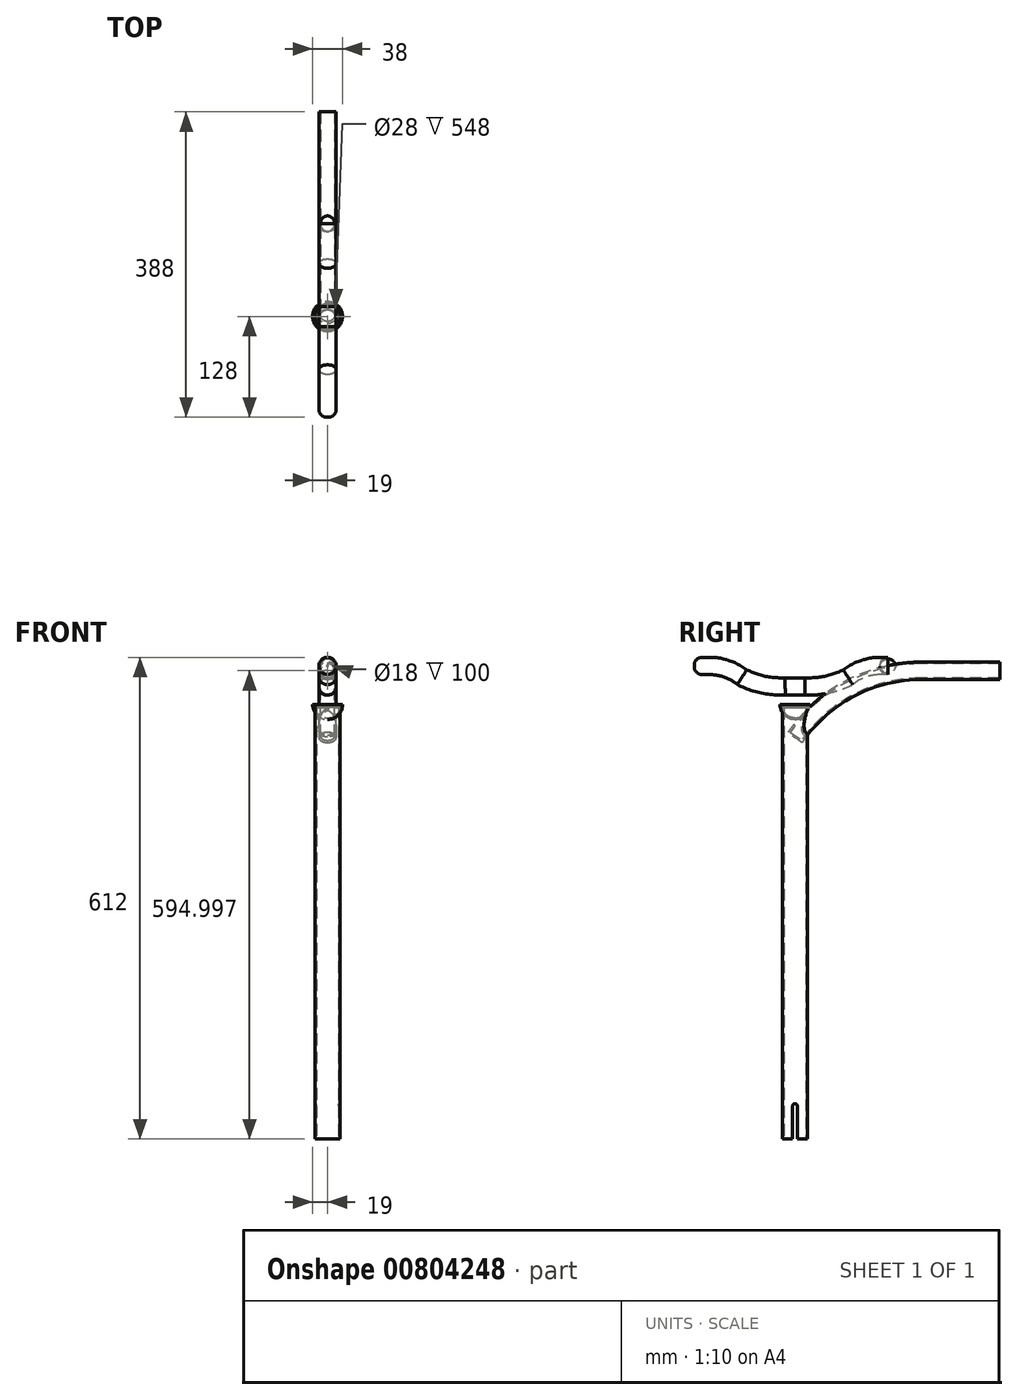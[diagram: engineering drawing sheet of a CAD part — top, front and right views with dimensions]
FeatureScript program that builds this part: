
annotation { "Feature Type Name" : "Feature", "Feature Type Description" : "" }
export const myFeature = defineFeature(function(context is Context, id is Id, definition is map)
    precondition{}
    {
        {
            var Q0;
            Q0=qCreatedBy(makeId("Top.planeOp"),FACE);
            var sketch = newSketch(context, id + "F0", { "sketchPlane" : qUnion([Q0])});
            skCircle(sketch, "E0", {"center": v(0, 0) * mm, "radius": 16 * mm});
            skSolve(sketch);
        }
        {
            var Q0;
            Q0 = qSketchRegion(id + "F0", true);
            extrude(context, id + "F1", {"entities" : qUnion([Q0]), "depth" : 550 * mm, "offsetDistance" : 25 * mm});
        }
        {
            var Q0;
            Q0=makeQuery(id+"F1.opExtrude","CAP_FACE",FACE,{"disambiguationData":[OSD([sQuery(id+"F0.wireOp",EDGE,"E0")])],"isStart":true});
            shell(context, id + "F2", {"entities" : qUnion([Q0]), "thickness" : 2 * mm});
        }
        {
            var Q0;
            Q0=qCreatedBy(makeId("Right.planeOp"),FACE);
            var sketch = newSketch(context, id + "F3", { "sketchPlane" : qUnion([Q0])});
            skLineSegment(sketch, "E1.bottom", {"start": v(-3, 0) * mm, "end": v(3, 0) * mm});
            skLineSegment(sketch, "E1.top", {"start": v(0, 45) * mm, "end": v(0, 45) * mm});
            skLineSegment(sketch, "E1.left", {"start": v(-3, 0) * mm, "end": v(-3, 42) * mm});
            skLineSegment(sketch, "E1.right", {"start": v(3, 0) * mm, "end": v(3, 42) * mm});
            skPoint(sketch, "E2.visualSharp", {"position": v(-3, 45) * mm});
            skArc(sketch, "E2.filletArc", {"start": v(0, 45) * mm, "mid": v(-2.12, 44.12) * mm, "end": v(-3, 42) * mm});
            skPoint(sketch, "E3.visualSharp", {"position": v(3, 45) * mm});
            skArc(sketch, "E3.filletArc", {"start": v(3, 42) * mm, "mid": v(2.12, 44.12) * mm, "end": v(0, 45) * mm});
            skSolve(sketch);
        }
        {
            var Q0;
            Q0 = qSketchRegion(id + "F3", true);
            extrude(context, id + "F4", {"entities" : qUnion([Q0]), "operationType" : NewBodyOperationType.REMOVE, "endBound" : BoundingType.SYMMETRIC, "depth" : 35 * mm, "offsetDistance" : 25 * mm});
        }
        {
            var Q0;
            Q0=qCreatedBy(makeId("Right.planeOp"),FACE);
            var sketch = newSketch(context, id + "F5", { "sketchPlane" : qUnion([Q0])});
            skArc(sketch, "E4", {"start": v(160, 595) * mm, "mid": v(69.53, 572.2) * mm, "end": v(0, 510) * mm});
            skLineSegment(sketch, "E5", {"start": v(160, 595) * mm, "end": v(260, 595) * mm});
            skLineSegment(sketch, "E6", {"start": v(0, 550) * mm, "end": v(0, 510) * mm, "construction": true});
            skSolve(sketch);
        }
        {
            var Q0;
            Q0=sQuery(id+"F5.wireOp",VERTEX,"E5.end");
            var Q1;
            Q1=qCreatedBy(makeId("Front.planeOp"),FACE);
            cPlane(context, id + "F6", {"entities" : qUnion([Q0, Q1]), "cplaneType" : CPlaneType.PLANE_POINT, "offset" : 25 * mm, "width" : 150 * mm, "height" : 150 * mm});
        }
        {
            var Q0;
            Q0=qCreatedBy(id+"F6.planeOp",FACE);
            var sketch = newSketch(context, id + "F7", { "sketchPlane" : qUnion([Q0])});
            skCircle(sketch, "E7", {"center": v(0, 595) * mm, "radius": 11 * mm});
            skSolve(sketch);
        }
        {
            var Q0;
            Q0 = qSketchRegion(id + "F7", true);
            var Q1;
            Q1 = qConstructionFilter(qBodyType(qCreatedBy(id + "F5" ,EDGE), BodyType.WIRE), ConstructionObject.NO);
            sweep(context, id + "F8", {"operationType" : NewBodyOperationType.ADD, "profiles" : qUnion([Q0]), "path" : qUnion([Q1])});
        }
        {
            var Q0;
            Q0=makeQuery(id+"F8.opSweep","CAP_FACE",FACE,{"disambiguationData":[OSD([sQuery(id+"F5.wireOp",VERTEX,"E5.end"),sQuery(id+"F7.wireOp",EDGE,"E7")])],"isStart":true});
            shell(context, id + "F9", {"entities" : qUnion([Q0]), "thickness" : 2 * mm});
        }
        {
            var Q0;
            Q0=qCreatedBy(makeId("Right.planeOp"),FACE);
            var sketch = newSketch(context, id + "F10", { "sketchPlane" : qUnion([Q0])});
            skLineSegment(sketch, "E8", {"start": v(0, 575) * mm, "end": v(0, 0) * mm, "construction": true});
            skLineSegment(sketch, "E9", {"start": v(-128, 601) * mm, "end": v(-108, 601) * mm});
            skArc(sketch, "E10", {"start": v(-67.24, 586.71) * mm, "mid": v(-86.4, 597.33) * mm, "end": v(-108, 601) * mm});
            skArc(sketch, "E11", {"start": v(-67.24, 586.71) * mm, "mid": v(-40.62, 577.38) * mm, "end": v(-12.5, 575) * mm});
            skLineSegment(sketch, "E12", {"start": v(-12.5, 575) * mm, "end": v(0, 575) * mm});
            skLineSegment(sketch, "E13.MirrorCS", {"start": v(12.5, 575) * mm, "end": v(0, 575) * mm});
            skArc(sketch, "E14.MirrorCS", {"start": v(67.24, 586.71) * mm, "mid": v(40.62, 577.38) * mm, "end": v(12.5, 575) * mm});
            skArc(sketch, "E15.MirrorCS", {"start": v(67.24, 586.71) * mm, "mid": v(86.4, 597.33) * mm, "end": v(108, 601) * mm});
            skLineSegment(sketch, "E16.MirrorCS", {"start": v(128, 601) * mm, "end": v(108, 601) * mm});
            skSolve(sketch);
        }
        {
            var Q0;
            Q0=sQuery(id+"F10.wireOp",VERTEX,"E16.MirrorCS.start");
            var Q1;
            Q1=qCreatedBy(id+"F6.planeOp",FACE);
            cPlane(context, id + "F11", {"entities" : qUnion([Q0, Q1]), "cplaneType" : CPlaneType.PLANE_POINT, "offset" : 25 * mm, "width" : 150 * mm, "height" : 150 * mm});
        }
        {
            var Q0;
            Q0=qCreatedBy(id+"F11.planeOp",FACE);
            var sketch = newSketch(context, id + "F12", { "sketchPlane" : qUnion([Q0])});
            skCircle(sketch, "E17", {"center": v(0, 601) * mm, "radius": 11 * mm});
            skSolve(sketch);
        }
        {
            var Q0;
            Q0 = qSketchRegion(id + "F12", true);
            var Q1;
            Q1 = qConstructionFilter(qBodyType(qCreatedBy(id + "F10" ,EDGE), BodyType.WIRE), ConstructionObject.NO);
            sweep(context, id + "F13", {"profiles" : qUnion([Q0]), "path" : qUnion([Q1])});
        }
        {
            var Q0;
            Q0=makeQuery(id+"F13.opSweep","CAP_EDGE",EDGE,{"disambiguationData":[OSD([sQuery(id+"F10.wireOp",VERTEX,"E9.start"),sQuery(id+"F12.wireOp",EDGE,"E17")])],"isStart":false});
            var Q1;
            Q1=makeQuery(id+"F13.opSweep","CAP_EDGE",EDGE,{"disambiguationData":[OSD([sQuery(id+"F10.wireOp",VERTEX,"E16.MirrorCS.start"),sQuery(id+"F12.wireOp",EDGE,"E17")])],"isStart":true});
            fillet(context, id + "F14", {"entities" : qUnion([Q0, Q1]), "radius" : 10 * mm, "tangentPropagation" : true, "allowEdgeOverflow" : false});
        }
        {
            var Q0;
            Q0=qCreatedBy(makeId("Right.planeOp"),FACE);
            var sketch = newSketch(context, id + "F15", { "sketchPlane" : qUnion([Q0])});
            skArc(sketch, "E18", {"start": v(-19, 552) * mm, "mid": v(-13.44, 538.56) * mm, "end": v(0, 533) * mm});
            skLineSegment(sketch, "E19", {"start": v(0, 552) * mm, "end": v(0, 533) * mm});
            skLineSegment(sketch, "E20", {"start": v(-19, 552) * mm, "end": v(0, 552) * mm});
            skPoint(sketch, "E21.orphan", {"position": v(0, 571) * mm});
            skSolve(sketch);
        }
        {
            var Q0;
            Q0 = qSketchRegion(id + "F15", true);
            var Q1;
            Q1=sQuery(id+"F15.wireOp",EDGE,"E19");
            revolve(context, id + "F16", {"surfaceOperationType" : NewSurfaceOperationType.NEW, "entities" : qUnion([Q0]), "axis" : qUnion([Q1]), "revolveType" : RevolveType.FULL});
        }
        {
            var Q0;
            Q0=makeQuery(id+"F16.opRevolve","SWEPT_FACE",FACE,{"disambiguationData":[OSD([sQuery(id+"F15.wireOp",EDGE,"E20")])]});
            shell(context, id + "F17", {"entities" : qUnion([Q0]), "thickness" : 2 * mm});
        }
    });
